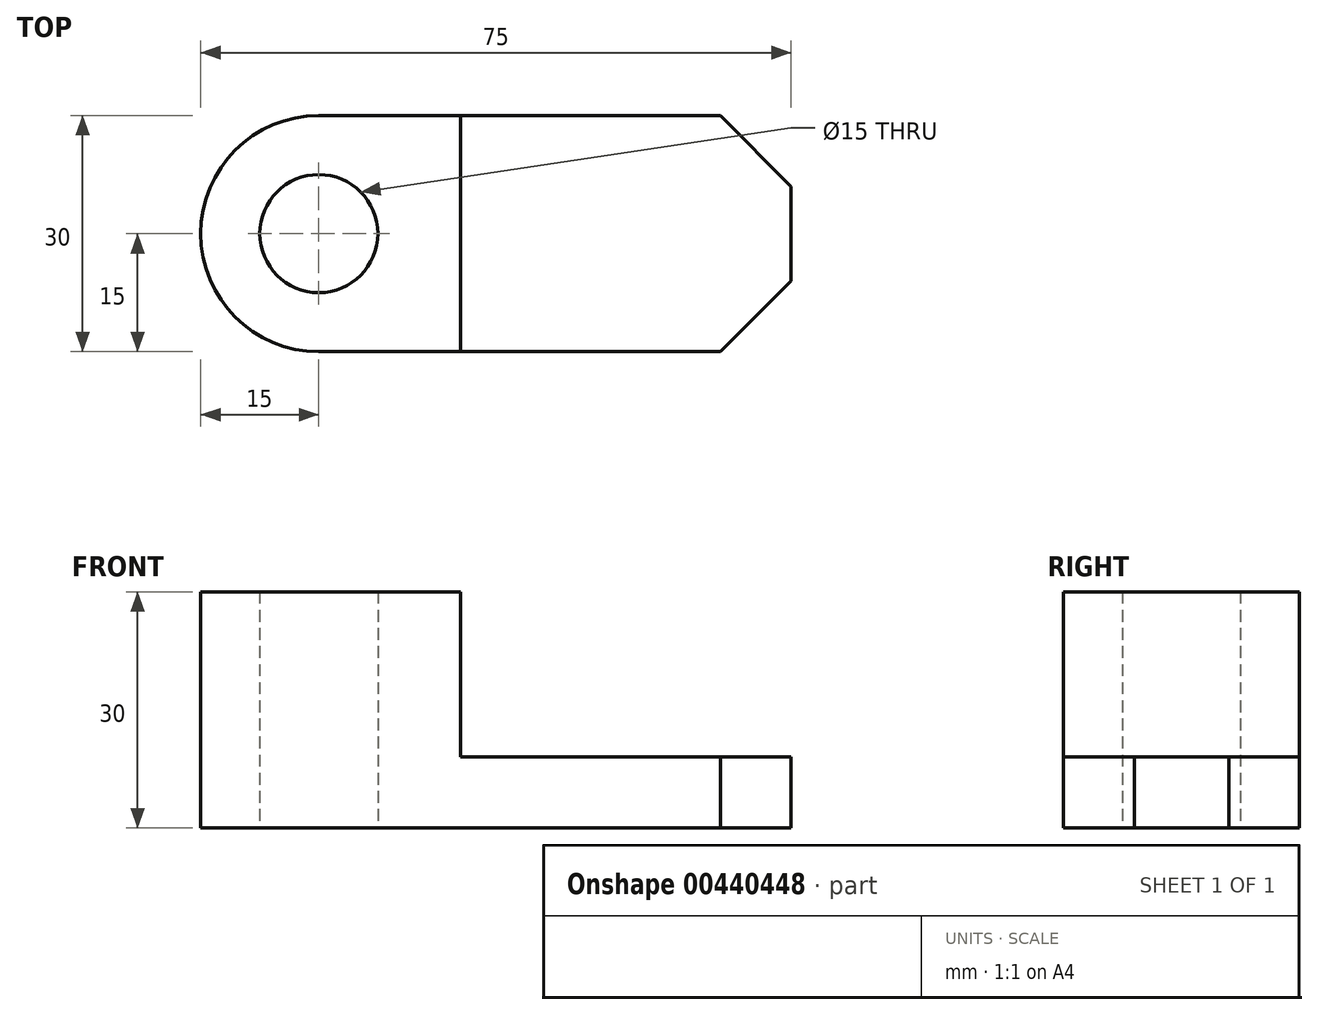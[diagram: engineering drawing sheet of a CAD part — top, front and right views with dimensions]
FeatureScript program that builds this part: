
annotation { "Feature Type Name" : "Feature", "Feature Type Description" : "" }
export const myFeature = defineFeature(function(context is Context, id is Id, definition is map)
    precondition{}
    {
        {
            var Q0;
            Q0=qCreatedBy(makeId("Top.planeOp"),FACE);
            var sketch = newSketch(context, id + "F0", { "sketchPlane" : qUnion([Q0])});
            skLineSegment(sketch, "E0", {"start": v(0, 0) * mm, "end": v(9, 9) * mm});
            skLineSegment(sketch, "E1", {"start": v(9, 9) * mm, "end": v(9, 21) * mm});
            skLineSegment(sketch, "E2", {"start": v(9, 21) * mm, "end": v(0, 30) * mm});
            skLineSegment(sketch, "E3", {"start": v(0, 30) * mm, "end": v(-51, 30) * mm});
            skLineSegment(sketch, "E4", {"start": v(-51, 0) * mm, "end": v(0, 0) * mm});
            skArc(sketch, "E5", {"start": v(-51, 30) * mm, "mid": v(-66, 15) * mm, "end": v(-51, 0) * mm});
            skLineSegment(sketch, "E6", {"start": v(-33, 30) * mm, "end": v(-33, 0) * mm});
            skCircle(sketch, "E7", {"center": v(-51, 15) * mm, "radius": 7.5 * mm});
            skLineSegment(sketch, "E8", {"start": v(9, 21) * mm, "end": v(9, 18.5) * mm});
            skLineSegment(sketch, "E9", {"start": v(9, 9) * mm, "end": v(9, 11.5) * mm});
            skLineSegment(sketch, "E10", {"start": v(9, 18.5) * mm, "end": v(-33, 18.5) * mm});
            skLineSegment(sketch, "E11", {"start": v(9, 11.5) * mm, "end": v(-33, 11.5) * mm});
            skSolve(sketch);
        }
        {
            var Q0;
            {var subQ4=sQuery(id+"F0.wireOp",EDGE,"E5");Q0=makeQuery(id+"F0.imprint","IMPRINT",FACE,{"disambiguationData":[TD([[makeQuery(id+"F0.imprint","IMPRINT",EDGE,{"derivedFrom":subQ4}),1.0]])]});}
            extrude(context, id + "F1", {"entities" : qUnion([Q0]), "depth" : 30 * mm});
        }
        {
            var Q0;
            {var subQ1=sQuery(id+"F0.wireOp",EDGE,"E0");Q0=makeQuery(id+"F0.imprint","IMPRINT",FACE,{"disambiguationData":[TD([[makeQuery(id+"F0.imprint","IMPRINT",EDGE,{"derivedFrom":subQ1}),1.0]])]});}
            var Q1;
            {var subQ4=sQuery(id+"F0.wireOp",EDGE,"E2");Q1=makeQuery(id+"F0.imprint","IMPRINT",FACE,{"disambiguationData":[TD([[makeQuery(id+"F0.imprint","IMPRINT",EDGE,{"derivedFrom":subQ4}),1.0]])]});}
            var Q2;
            Q2=makeQuery(id+"F0.imprint","IMPRINT",FACE,{"disambiguationData":[TD([[makeQuery(id+"F0.imprint","IMPRINT",EDGE,{"derivedFrom":sQuery(id+"F0.wireOp",EDGE,"E1")}),1.0]])]});
            extrude(context, id + "F2", {"entities" : qUnion([Q0, Q1, Q2]), "operationType" : NewBodyOperationType.ADD, "depth" : 9 * mm});
        }
    });
